# Revit family: SH -770A-10W
name_source: partatom
category: Lighting Fixtures
revit_build: Autodesk Revit 2017 (Build: 20160225_1515(x64)
units: mm (PartAtom-declared; Revit-internal decimal feet)

## family parameters
Always vertical = Yes
Cut with Voids When Loaded = No
Host = Wall
Light Source = Yes
OmniClass Number = 23.80.70.00
OmniClass Title = Lighting
Part Type = Normal
Room Calculation Point = No
Round Connector Dimension = Use Diameter
Shared = Yes

## types (2) — shared parameters
Body Material = Aluminum
Color Filter = 16777215
Cunsumption current = 0 A
Dimming Lamp Color Temperature Shift = <None>
Emit from Line Length = 30.0 cm
IP = IP20
Instalation = Wall mounted
Lamp = LED
Light Source Symbol Size = 20.0 cm
Manufacturer = SHOA
Model = SH-770A-10w
Protection Class = class I
Type medule = SMD
URL = https://www.shoaco.com
Voltage/Frequency = 230V/50HZ
Website = www.shoaco.com
color temperature = 4000K
wattage = 10 W
zero-valued in all types: Cost

## per-type parameters (varying)
| type | Body color |
| SH-770A-10W-Aluminum(Black color-4000K-LED) | White |
| SH-770A-10W-Aluminum(Gold color-4000K-LED) | Gold color |

## geometry (parser evidence)
native form markers: Sweep x2
no freeform markers — native parametric forms only
